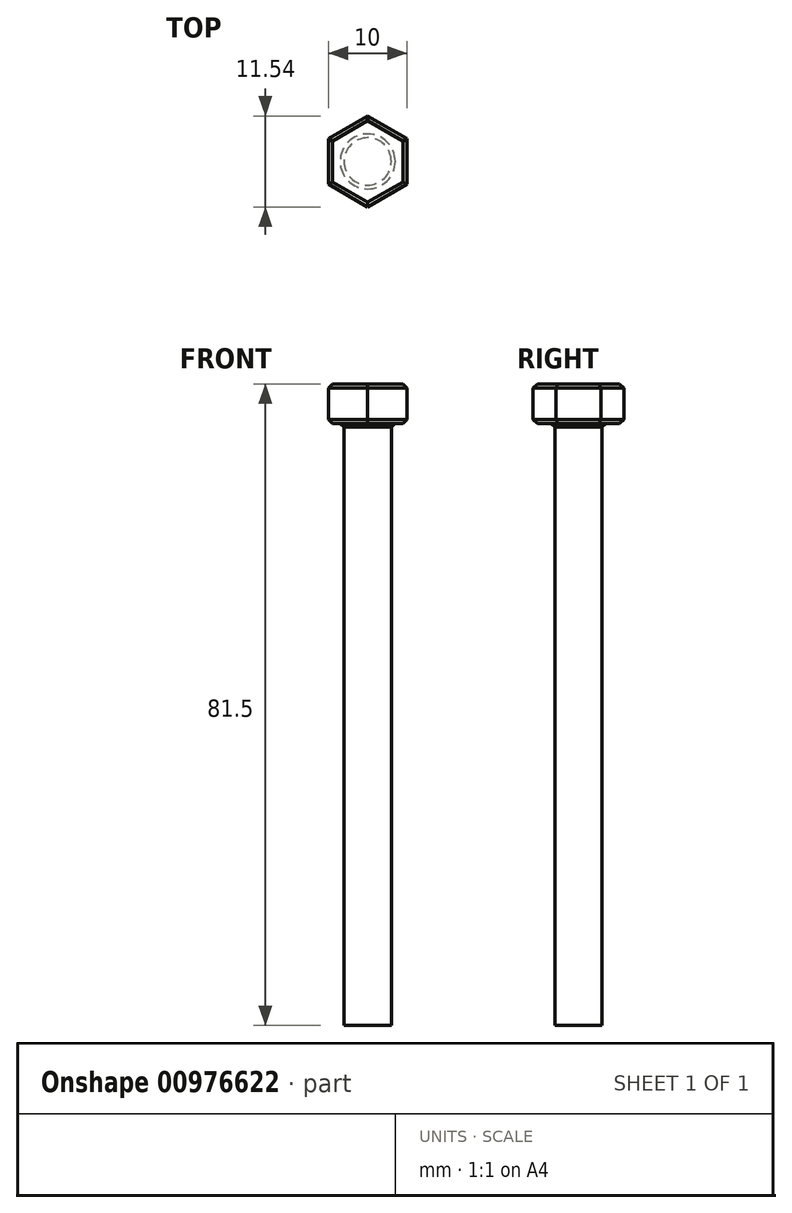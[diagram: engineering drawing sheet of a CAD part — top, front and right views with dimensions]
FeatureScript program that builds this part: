
annotation { "Feature Type Name" : "Feature", "Feature Type Description" : "" }
export const myFeature = defineFeature(function(context is Context, id is Id, definition is map)
    precondition{}
    {
        {
            var Q0;
            Q0=qCreatedBy(makeId("Top.planeOp"),FACE);
            var sketch = newSketch(context, id + "F0", { "sketchPlane" : qUnion([Q0])});
            skCircle(sketch, "E0", {"center": v(0, 0) * mm, "radius": 3 * mm});
            skSolve(sketch);
        }
        {
            var Q0;
            Q0=makeQuery(id+"F0.imprint","IMPRINT",FACE,{"disambiguationData":[TD([[makeQuery(id+"F0.imprint","IMPRINT",EDGE,{"derivedFrom":sQuery(id+"F0.wireOp",EDGE,"E0")}),1.0]])]});
            extrude(context, id + "F1", {"entities" : qUnion([Q0]), "depth" : 20 * mm, "offsetDistance" : 25 * mm});
        }
        {
            var Q0;
            Q0=makeQuery(id+"F1.opExtrude","CAP_FACE",FACE,{"disambiguationData":[OSD([sQuery(id+"F0.wireOp",EDGE,"E0")])],"isStart":false});
            var sketch = newSketch(context, id + "F2", { "sketchPlane" : qUnion([Q0])});
            skCircle(sketch, "E1.cCircle", {"center": v(0, 0) * mm, "radius": 5 * mm, "construction": true});
            skLineSegment(sketch, "E1.0", {"start": v(5, -2.89) * mm, "end": v(0, -5.77) * mm});
            skLineSegment(sketch, "E1.1", {"start": v(0, -5.77) * mm, "end": v(-5, -2.89) * mm});
            skLineSegment(sketch, "E1.2", {"start": v(-5, -2.89) * mm, "end": v(-5, 2.89) * mm});
            skLineSegment(sketch, "E1.3", {"start": v(-5, 2.89) * mm, "end": v(0, 5.77) * mm});
            skLineSegment(sketch, "E1.4", {"start": v(0, 5.77) * mm, "end": v(5, 2.89) * mm});
            skLineSegment(sketch, "E1.5", {"start": v(5, 2.89) * mm, "end": v(5, -2.89) * mm});
            skPoint(sketch, "E1.0.midPoint", {"position": v(2.5, -4.33) * mm});
            skSolve(sketch);
        }
        {
            var Q0;
            Q0=qSketchRegion(id+"F2",true);
            extrude(context, id + "F3", {"entities" : qUnion([Q0]), "operationType" : NewBodyOperationType.ADD, "depth" : 5 * mm, "offsetDistance" : 25 * mm});
        }
        {
            var Q0;
            Q0=makeQuery(id+"F3.opExtrude","CAP_EDGE",EDGE,{"disambiguationData":[OSD([sQuery(id+"F2.wireOp",EDGE,"E1.1")])],"isStart":false});
            var Q1;
            Q1=makeQuery(id+"F3.opExtrude","CAP_EDGE",EDGE,{"disambiguationData":[OSD([sQuery(id+"F2.wireOp",EDGE,"E1.0")])],"isStart":false});
            var Q2;
            Q2=makeQuery(id+"F3.opExtrude","CAP_EDGE",EDGE,{"disambiguationData":[OSD([sQuery(id+"F2.wireOp",EDGE,"E1.5")])],"isStart":false});
            var Q3;
            Q3=makeQuery(id+"F3.opExtrude","CAP_EDGE",EDGE,{"disambiguationData":[OSD([sQuery(id+"F2.wireOp",EDGE,"E1.4")])],"isStart":false});
            var Q4;
            Q4=makeQuery(id+"F3.opExtrude","CAP_EDGE",EDGE,{"disambiguationData":[OSD([sQuery(id+"F2.wireOp",EDGE,"E1.3")])],"isStart":false});
            var Q5;
            Q5=makeQuery(id+"F3.opExtrude","CAP_EDGE",EDGE,{"disambiguationData":[OSD([sQuery(id+"F2.wireOp",EDGE,"E1.2")])],"isStart":false});
            var Q6;
            Q6=makeQuery(id+"F3.opExtrude","CAP_FACE",FACE,{"disambiguationData":[OSD([sQuery(id+"F2.wireOp",EDGE,"E1.0"),sQuery(id+"F2.wireOp",EDGE,"E1.1"),sQuery(id+"F2.wireOp",EDGE,"E1.2"),sQuery(id+"F2.wireOp",EDGE,"E1.3"),sQuery(id+"F2.wireOp",EDGE,"E1.4"),sQuery(id+"F2.wireOp",EDGE,"E1.5")])],"isStart":true});
            chamfer(context, id + "F4", {"entities" : qUnion([Q0, Q1, Q2, Q3, Q4, Q5, Q6]), "width" : .5 * mm, "tangentPropagation" : true});
        }
        {
            var Q0;
            Q0=makeQuery(id+"F1.opExtrude","CAP_FACE",FACE,{"disambiguationData":[OSD([sQuery(id+"F0.wireOp",EDGE,"E0")])],"isStart":true});
            extrude(context, id + "F5", {"entities" : qUnion([Q0]), "operationType" : NewBodyOperationType.ADD, "depth" : 56.5 * mm, "offsetDistance" : 25 * mm});
        }
    });
